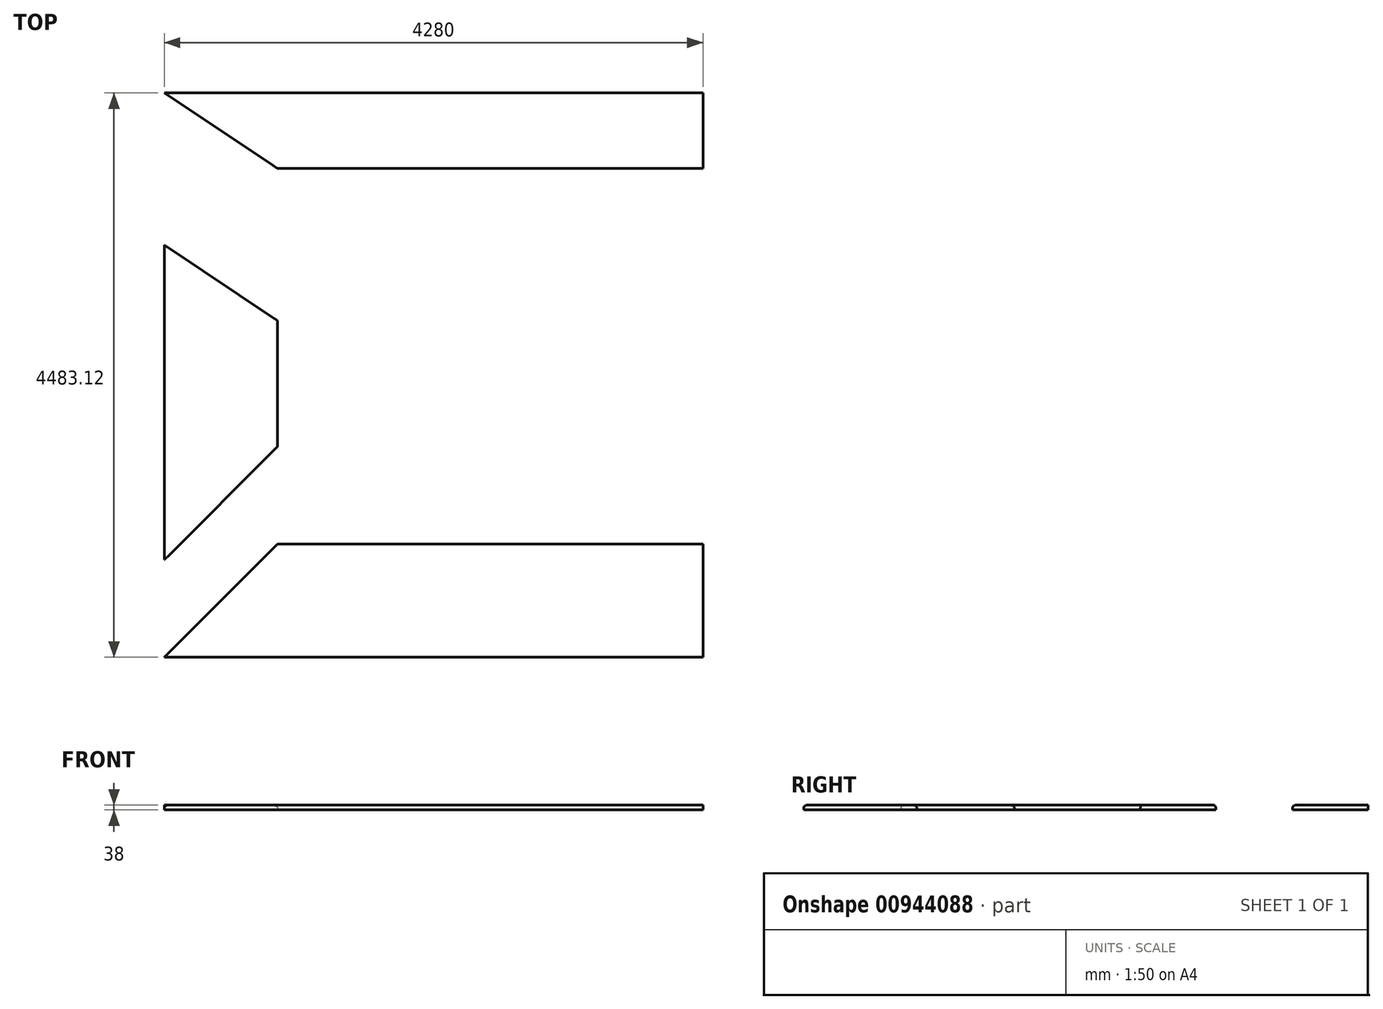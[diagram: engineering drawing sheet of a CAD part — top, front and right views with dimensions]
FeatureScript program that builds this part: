
annotation { "Feature Type Name" : "Feature", "Feature Type Description" : "" }
export const myFeature = defineFeature(function(context is Context, id is Id, definition is map)
    precondition{}
    {
        {
            var Q0;
            Q0=qCreatedBy(makeId("Top.planeOp"),FACE);
            var sketch = newSketch(context, id + "F0", { "sketchPlane" : qUnion([Q0])});
            skLineSegment(sketch, "E0.bottom", {"start": v(-3448.44, 1024.16) * mm, "end": v(-68.44, 1024.16) * mm});
            skLineSegment(sketch, "E0.top", {"start": v(-4348.44, 1624.16) * mm, "end": v(-68.44, 1624.16) * mm});
            skLineSegment(sketch, "E0.right", {"start": v(-68.44, 1024.16) * mm, "end": v(-68.44, 1624.16) * mm});
            skPoint(sketch, "E0.middle", {"position": v(-2208.44, 1324.16) * mm});
            skLineSegment(sketch, "E1.left", {"start": v(-4348.44, -2084.48) * mm, "end": v(-4348.44, 415.52) * mm});
            skLineSegment(sketch, "E1.right", {"start": v(-3448.44, -1184.48) * mm, "end": v(-3448.44, -184.48) * mm});
            skPoint(sketch, "E1.middle", {"position": v(-3898.44, -834.48) * mm});
            skLineSegment(sketch, "E2", {"start": v(-4348.44, 1624.16) * mm, "end": v(-3448.44, 1024.16) * mm});
            skLineSegment(sketch, "E3", {"start": v(-4348.44, 415.52) * mm, "end": v(-3448.44, -184.48) * mm});
            skLineSegment(sketch, "E4.bottom", {"start": v(-4348.44, -2858.96) * mm, "end": v(-68.44, -2858.96) * mm});
            skLineSegment(sketch, "E4.top", {"start": v(-3448.44, -1958.96) * mm, "end": v(-68.44, -1958.96) * mm});
            skLineSegment(sketch, "E4.right", {"start": v(-68.44, -2858.96) * mm, "end": v(-68.44, -1958.96) * mm});
            skPoint(sketch, "E4.middle", {"position": v(-2208.44, -2408.96) * mm});
            skLineSegment(sketch, "E5", {"start": v(-4348.44, -2858.96) * mm, "end": v(-3448.44, -1958.96) * mm});
            skLineSegment(sketch, "E6", {"start": v(-4348.44, -2084.48) * mm, "end": v(-3448.44, -1184.48) * mm});
            skPoint(sketch, "E1.bottom.end.orphan", {"position": v(-3448.44, -2084.48) * mm});
            skPoint(sketch, "E4.left.end.orphan", {"position": v(-4348.44, -1958.96) * mm});
            skSolve(sketch);
        }
        {
            var Q0;
            Q0 = qSketchRegion(id + "F0", true);
            extrude(context, id + "F1", {"entities" : qUnion([Q0]), "depth" : 38 * mm, "offsetDistance" : 25 * mm});
        }
        {
            var Q0;
            Q0=makeQuery(id+"F1.opExtrude","CAP_EDGE",EDGE,{"disambiguationData":[OSD([sQuery(id+"F0.wireOp",EDGE,"E0.bottom")])],"isStart":false});
            fillet(context, id + "F2", {"entities" : qUnion([Q0]), "radius" : 25 * mm, "tangentPropagation" : true, "allowEdgeOverflow" : false});
        }
        {
            var Q0;
            Q0=makeQuery(id+"F1.opExtrude","CAP_EDGE",EDGE,{"disambiguationData":[OSD([sQuery(id+"F0.wireOp",EDGE,"E1.right")])],"isStart":false});
            var Q1;
            Q1=makeQuery(id+"F1.opExtrude","CAP_EDGE",EDGE,{"disambiguationData":[OSD([sQuery(id+"F0.wireOp",EDGE,"E1.left")])],"isStart":false});
            fillet(context, id + "F3", {"entities" : qUnion([Q0, Q1]), "radius" : 25 * mm, "tangentPropagation" : true, "allowEdgeOverflow" : false});
        }
        {
            var Q0;
            Q0=makeQuery(id+"F1.opExtrude","CAP_EDGE",EDGE,{"disambiguationData":[OSD([sQuery(id+"F0.wireOp",EDGE,"E4.bottom")])],"isStart":false});
            var Q1;
            Q1=makeQuery(id+"F1.opExtrude","CAP_EDGE",EDGE,{"disambiguationData":[OSD([sQuery(id+"F0.wireOp",EDGE,"E4.top")])],"isStart":false});
            fillet(context, id + "F4", {"entities" : qUnion([Q0, Q1]), "radius" : 25 * mm, "tangentPropagation" : true, "allowEdgeOverflow" : false});
        }
    });
